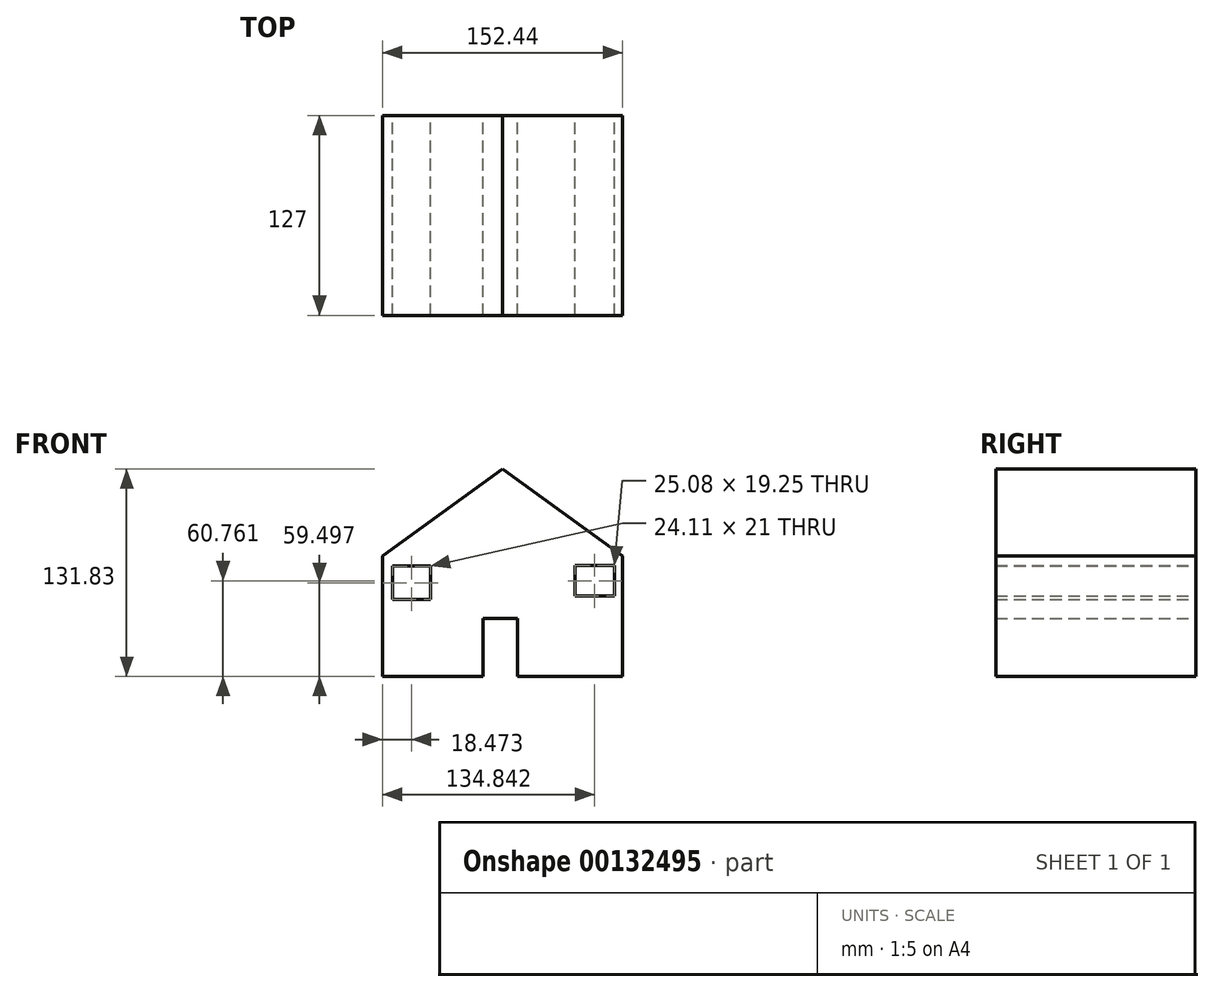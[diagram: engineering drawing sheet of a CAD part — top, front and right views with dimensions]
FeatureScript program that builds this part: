
annotation { "Feature Type Name" : "Feature", "Feature Type Description" : "" }
export const myFeature = defineFeature(function(context is Context, id is Id, definition is map)
    precondition{}
    {
        {
            var Q0;
            Q0=qCreatedBy(makeId("Front.planeOp"),FACE);
            var sketch = newSketch(context, id + "F0", { "sketchPlane" : qUnion([Q0])});
            skLineSegment(sketch, "E0", {"start": v(-76.22, 0) * mm, "end": v(-76.22, -76.51) * mm});
            skLineSegment(sketch, "E1", {"start": v(-76.22, -76.51) * mm, "end": v(76.22, -76.51) * mm});
            skLineSegment(sketch, "E2", {"start": v(76.22, -76.51) * mm, "end": v(76.22, 0) * mm});
            skLineSegment(sketch, "E3", {"start": v(76.22, 0) * mm, "end": v(-76.22, 0) * mm});
            skLineSegment(sketch, "E4", {"start": v(-76.22, 0) * mm, "end": v(0, 55.32) * mm});
            skLineSegment(sketch, "E5", {"start": v(0, 55.32) * mm, "end": v(76.22, 0) * mm});
            skLineSegment(sketch, "E6.bottom", {"start": v(-69.8, -6.51) * mm, "end": v(-45.7, -6.51) * mm});
            skLineSegment(sketch, "E6.top", {"start": v(-69.8, -27.51) * mm, "end": v(-45.7, -27.51) * mm});
            skLineSegment(sketch, "E6.left", {"start": v(-69.8, -6.51) * mm, "end": v(-69.8, -27.51) * mm});
            skLineSegment(sketch, "E6.right", {"start": v(-45.7, -6.51) * mm, "end": v(-45.7, -27.51) * mm});
            skLineSegment(sketch, "E7.bottom", {"start": v(-12.44, -39.76) * mm, "end": v(9.53, -39.76) * mm});
            skLineSegment(sketch, "E7.top", {"start": v(-12.44, -76.51) * mm, "end": v(9.53, -76.51) * mm});
            skLineSegment(sketch, "E7.left", {"start": v(-12.44, -39.76) * mm, "end": v(-12.44, -76.51) * mm});
            skLineSegment(sketch, "E7.right", {"start": v(9.53, -39.76) * mm, "end": v(9.53, -76.51) * mm});
            skLineSegment(sketch, "E8.bottom", {"start": v(71.16, -6.12) * mm, "end": v(46.08, -6.12) * mm});
            skLineSegment(sketch, "E8.top", {"start": v(71.16, -25.37) * mm, "end": v(46.08, -25.37) * mm});
            skLineSegment(sketch, "E8.left", {"start": v(71.16, -6.12) * mm, "end": v(71.16, -25.37) * mm});
            skLineSegment(sketch, "E8.right", {"start": v(46.08, -6.12) * mm, "end": v(46.08, -25.37) * mm});
            skSolve(sketch);
        }
        {
            var Q0;
            Q0=makeQuery(id+"F0.imprint","IMPRINT",FACE,{"disambiguationData":[TD([[makeQuery(id+"F0.imprint","IMPRINT",EDGE,{"derivedFrom":sQuery(id+"F0.wireOp",EDGE,"E3")}),-1.0]])]});
            var Q1;
            {var subQ0=sQuery(id+"F0.wireOp",EDGE,"E0");Q1=makeQuery(id+"F0.imprint","IMPRINT",FACE,{"disambiguationData":[TD([[makeQuery(id+"F0.imprint","IMPRINT",EDGE,{"derivedFrom":subQ0}),1.0]])]});}
            extrude(context, id + "F1", {"entities" : qUnion([Q0, Q1]), "depth" : 127 * mm});
        }
    });
